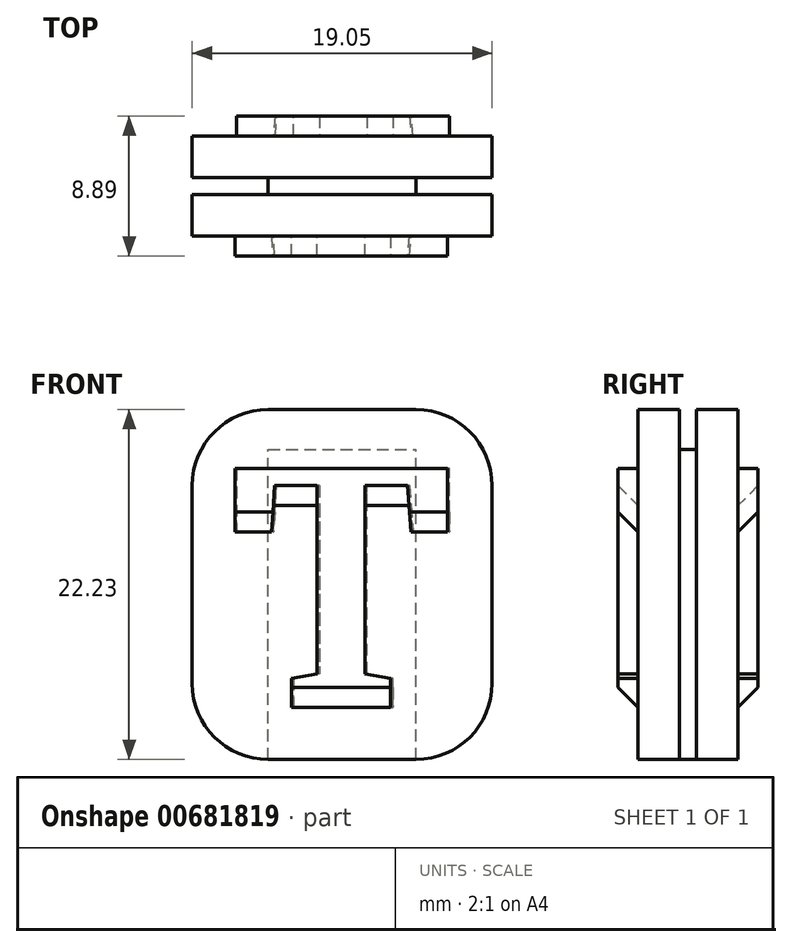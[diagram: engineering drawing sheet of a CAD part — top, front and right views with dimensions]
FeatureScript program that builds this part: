
annotation { "Feature Type Name" : "Feature", "Feature Type Description" : "" }
export const myFeature = defineFeature(function(context is Context, id is Id, definition is map)
    precondition{}
    {
        {
            var Q0;
            Q0=qCreatedBy(makeId("Front.planeOp"),FACE);
            var sketch = newSketch(context, id + "F0", { "sketchPlane" : qUnion([Q0])});
            skLineSegment(sketch, "E0.bottom", {"start": v(0, 0) * mm, "end": v(19.05, 0) * mm});
            skLineSegment(sketch, "E0.top", {"start": v(0, 22.23) * mm, "end": v(19.05, 22.23) * mm});
            skLineSegment(sketch, "E0.left", {"start": v(0, 0) * mm, "end": v(0, 22.23) * mm});
            skLineSegment(sketch, "E0.right", {"start": v(19.05, 0) * mm, "end": v(19.05, 22.23) * mm});
            skSolve(sketch);
        }
        {
            var Q0;
            Q0=makeQuery(id+"F0.imprint","IMPRINT",FACE,{"disambiguationData":[TD([[makeQuery(id+"F0.imprint","IMPRINT",EDGE,{"derivedFrom":sQuery(id+"F0.wireOp",EDGE,"E0.bottom")}),1.0]])]});
            extrude(context, id + "F1", {"entities" : qUnion([Q0]), "depth" : 6.35 * mm, "offsetDistance" : 25.4 * mm});
        }
        {
            var Q0;
            Q0=makeQuery(id+"F1.opExtrude","CAP_FACE",FACE,{"disambiguationData":[OSD([sQuery(id+"F0.wireOp",EDGE,"E0.bottom"),sQuery(id+"F0.wireOp",EDGE,"E0.top"),sQuery(id+"F0.wireOp",EDGE,"E0.left"),sQuery(id+"F0.wireOp",EDGE,"E0.right")])],"isStart":false});
            var sketch = newSketch(context, id + "F2", { "sketchPlane" : qUnion([Q0])});
            skText(sketch, "E1", { "text": "T", "fontName": "RobotoSlab-Bold.ttf"});
            skPoint(sketch, "E2", {"position": v(19.05, 11.11) * mm});
            const initialGuessF2  = {"E1": [0.00229, 0.00331, 1, 0, 0.01536]};
            skSetInitialGuess(sketch, initialGuessF2);
            skSolve(sketch);
        }
        {
            var Q0;
            Q0=makeQuery(id+"F1.opExtrude","CAP_FACE",FACE,{"disambiguationData":[OSD([sQuery(id+"F0.wireOp",EDGE,"E0.bottom"),sQuery(id+"F0.wireOp",EDGE,"E0.top"),sQuery(id+"F0.wireOp",EDGE,"E0.left"),sQuery(id+"F0.wireOp",EDGE,"E0.right")])],"isStart":true});
            var sketch = newSketch(context, id + "F3", { "sketchPlane" : qUnion([Q0])});
            skText(sketch, "E3", { "text": "T", "fontName": "RobotoSlab-Bold.ttf"});
            const initialGuessF3  = {"E3": [-0.01676, 0.00331, 1, 0, 0.01536]};
            skSetInitialGuess(sketch, initialGuessF3);
            skSolve(sketch);
        }
        {
            var Q0;
            Q0=makeQuery(id+"F1.opExtrude","SWEPT_FACE",FACE,{"disambiguationData":[OSD([sQuery(id+"F0.wireOp",EDGE,"E0.top")])]});
            var sketch = newSketch(context, id + "F4", { "sketchPlane" : qUnion([Q0])});
            skLineSegment(sketch, "E4.bottom", {"start": v(0, -2.64) * mm, "end": v(19.05, -2.64) * mm});
            skLineSegment(sketch, "E4.top", {"start": v(0, -3.7) * mm, "end": v(19.05, -3.7) * mm});
            skLineSegment(sketch, "E4.left", {"start": v(0, -2.64) * mm, "end": v(0, -3.7) * mm});
            skLineSegment(sketch, "E4.right", {"start": v(19.05, -2.64) * mm, "end": v(19.05, -3.7) * mm});
            skLineSegment(sketch, "E5", {"start": v(4.83, -2.64) * mm, "end": v(4.83, -3.7) * mm});
            skLineSegment(sketch, "E6", {"start": v(14.22, -2.64) * mm, "end": v(14.22, -3.7) * mm});
            skSolve(sketch);
        }
        {
            var Q0;
            {var subQ0=sQuery(id+"F4.wireOp",EDGE,"E4.left");Q0=makeQuery(id+"F4.imprint","IMPRINT",FACE,{"disambiguationData":[TD([[makeQuery(id+"F4.imprint","IMPRINT",EDGE,{"derivedFrom":subQ0}),-1.0]])]});}
            var Q1;
            {var subQ0=sQuery(id+"F4.wireOp",EDGE,"E4.right");Q1=makeQuery(id+"F4.imprint","IMPRINT",FACE,{"disambiguationData":[TD([[makeQuery(id+"F4.imprint","IMPRINT",EDGE,{"derivedFrom":subQ0}),1.0]])]});}
            extrude(context, id + "F5", {"entities" : qUnion([Q0, Q1]), "operationType" : NewBodyOperationType.REMOVE, "oppositeDirection" : true, "depth" : 25.4 * mm, "offsetDistance" : 25.4 * mm});
        }
        {
            var Q0;
            Q0=makeQuery(id+"F1.opExtrude","SWEPT_FACE",FACE,{"disambiguationData":[OSD([sQuery(id+"F0.wireOp",EDGE,"E0.top")])]});
            var sketch = newSketch(context, id + "F6", { "sketchPlane" : qUnion([Q0])});
            skLineSegment(sketch, "E7.bottom", {"start": v(4.83, -2.64) * mm, "end": v(14.22, -2.64) * mm});
            skLineSegment(sketch, "E7.top", {"start": v(4.83, -3.7) * mm, "end": v(14.22, -3.7) * mm});
            skLineSegment(sketch, "E7.left", {"start": v(4.83, -2.64) * mm, "end": v(4.83, -3.7) * mm});
            skLineSegment(sketch, "E7.right", {"start": v(14.22, -2.64) * mm, "end": v(14.22, -3.7) * mm});
            skSolve(sketch);
        }
        {
            var Q0;
            Q0=makeQuery(id+"F6.imprint","IMPRINT",FACE,{"disambiguationData":[TD([[makeQuery(id+"F6.imprint","IMPRINT",EDGE,{"derivedFrom":sQuery(id+"F6.wireOp",EDGE,"E7.bottom")}),-1.0]])]});
            extrude(context, id + "F7", {"entities" : qUnion([Q0]), "operationType" : NewBodyOperationType.REMOVE, "oppositeDirection" : true, "depth" : 2.54 * mm, "offsetDistance" : 25.4 * mm});
        }
        {
            var Q0;
            {var subQ0=sQuery(id+"F0.wireOp",EDGE,"E0.bottom");var subQ1=sQuery(id+"F0.wireOp",EDGE,"E0.left");var subQ3=sQuery(id+"F4.wireOp",EDGE,"E4.bottom");Q0=makeQuery(id+"F5.boolean.opBoolean","SPLIT",EDGE,{"disambiguationData":[TD([makeQuery(id+"F5.opExtrude","SWEPT_FACE",FACE,{"disambiguationData":[OSD([subQ3]),TDD([makeQuery(id+"F4.imprint","IMPRINT",EDGE,{"disambiguationData":[TD([[makeQuery(id+"F4.imprint","INTERSECT",VERTEX,{"derivedFrom":[subQ3,sQuery(id+"F4.wireOp",EDGE,"E5")]}),1.0]])],"derivedFrom":subQ3})])]})])],"derivedFrom":makeQuery(id+"F1.opExtrude","SWEPT_EDGE",EDGE,{"disambiguationData":[OSD([subQ0,subQ1])]})});}
            var Q1;
            {var subQ0=sQuery(id+"F0.wireOp",EDGE,"E0.bottom");var subQ1=sQuery(id+"F0.wireOp",EDGE,"E0.left");var subQ3=sQuery(id+"F4.wireOp",EDGE,"E4.top");Q1=makeQuery(id+"F5.boolean.opBoolean","SPLIT",EDGE,{"disambiguationData":[TD([makeQuery(id+"F5.opExtrude","SWEPT_FACE",FACE,{"disambiguationData":[OSD([subQ3]),TDD([makeQuery(id+"F4.imprint","IMPRINT",EDGE,{"disambiguationData":[TD([[makeQuery(id+"F4.imprint","INTERSECT",VERTEX,{"derivedFrom":[subQ3,sQuery(id+"F4.wireOp",EDGE,"E5")]}),1.0]])],"derivedFrom":subQ3})])]})])],"derivedFrom":makeQuery(id+"F1.opExtrude","SWEPT_EDGE",EDGE,{"disambiguationData":[OSD([subQ0,subQ1])]})});}
            var Q2;
            {var subQ0=sQuery(id+"F0.wireOp",EDGE,"E0.left");var subQ1=sQuery(id+"F0.wireOp",EDGE,"E0.top");var subQ2=sQuery(id+"F4.wireOp",EDGE,"E4.top");var subQ3=makeQuery(id+"F1.opExtrude","SWEPT_EDGE",EDGE,{"disambiguationData":[OSD([subQ1,subQ0])]});Q2=makeQuery(id+"F5.boolean.opBoolean","SPLIT",EDGE,{"disambiguationData":[TD([makeQuery(id+"F5.opExtrude","SWEPT_FACE",FACE,{"disambiguationData":[OSD([subQ2]),TDD([makeQuery(id+"F4.imprint","IMPRINT",EDGE,{"disambiguationData":[TD([[makeQuery(id+"F4.imprint","INTERSECT",VERTEX,{"derivedFrom":[subQ2,sQuery(id+"F4.wireOp",EDGE,"E5")]}),1.0]])],"derivedFrom":subQ2})])]})])],"derivedFrom":subQ3});}
            var Q3;
            {var subQ0=sQuery(id+"F0.wireOp",EDGE,"E0.left");var subQ1=sQuery(id+"F0.wireOp",EDGE,"E0.top");var subQ2=sQuery(id+"F4.wireOp",EDGE,"E4.bottom");var subQ3=makeQuery(id+"F1.opExtrude","SWEPT_EDGE",EDGE,{"disambiguationData":[OSD([subQ1,subQ0])]});Q3=makeQuery(id+"F5.boolean.opBoolean","SPLIT",EDGE,{"disambiguationData":[TD([makeQuery(id+"F5.opExtrude","SWEPT_FACE",FACE,{"disambiguationData":[OSD([subQ2]),TDD([makeQuery(id+"F4.imprint","IMPRINT",EDGE,{"disambiguationData":[TD([[makeQuery(id+"F4.imprint","INTERSECT",VERTEX,{"derivedFrom":[subQ2,sQuery(id+"F4.wireOp",EDGE,"E5")]}),1.0]])],"derivedFrom":subQ2})])]})])],"derivedFrom":subQ3});}
            var Q4;
            {var subQ0=sQuery(id+"F0.wireOp",EDGE,"E0.right");var subQ1=sQuery(id+"F0.wireOp",EDGE,"E0.top");var subQ2=sQuery(id+"F4.wireOp",EDGE,"E4.bottom");var subQ3=makeQuery(id+"F1.opExtrude","SWEPT_EDGE",EDGE,{"disambiguationData":[OSD([subQ1,subQ0])]});Q4=makeQuery(id+"F5.boolean.opBoolean","SPLIT",EDGE,{"disambiguationData":[TD([makeQuery(id+"F5.opExtrude","SWEPT_FACE",FACE,{"disambiguationData":[OSD([subQ2]),TDD([makeQuery(id+"F4.imprint","IMPRINT",EDGE,{"disambiguationData":[TD([[makeQuery(id+"F4.imprint","INTERSECT",VERTEX,{"derivedFrom":[subQ2,sQuery(id+"F4.wireOp",EDGE,"E6")]}),-1.0]])],"derivedFrom":subQ2})])]})])],"derivedFrom":subQ3});}
            var Q5;
            {var subQ0=sQuery(id+"F0.wireOp",EDGE,"E0.right");var subQ1=sQuery(id+"F0.wireOp",EDGE,"E0.top");var subQ2=sQuery(id+"F4.wireOp",EDGE,"E4.top");var subQ3=makeQuery(id+"F1.opExtrude","SWEPT_EDGE",EDGE,{"disambiguationData":[OSD([subQ1,subQ0])]});Q5=makeQuery(id+"F5.boolean.opBoolean","SPLIT",EDGE,{"disambiguationData":[TD([makeQuery(id+"F5.opExtrude","SWEPT_FACE",FACE,{"disambiguationData":[OSD([subQ2]),TDD([makeQuery(id+"F4.imprint","IMPRINT",EDGE,{"disambiguationData":[TD([[makeQuery(id+"F4.imprint","INTERSECT",VERTEX,{"derivedFrom":[subQ2,sQuery(id+"F4.wireOp",EDGE,"E6")]}),-1.0]])],"derivedFrom":subQ2})])]})])],"derivedFrom":subQ3});}
            var Q6;
            {var subQ0=sQuery(id+"F0.wireOp",EDGE,"E0.bottom");var subQ1=sQuery(id+"F0.wireOp",EDGE,"E0.right");var subQ3=sQuery(id+"F4.wireOp",EDGE,"E4.top");Q6=makeQuery(id+"F5.boolean.opBoolean","SPLIT",EDGE,{"disambiguationData":[TD([makeQuery(id+"F5.opExtrude","SWEPT_FACE",FACE,{"disambiguationData":[OSD([subQ3]),TDD([makeQuery(id+"F4.imprint","IMPRINT",EDGE,{"disambiguationData":[TD([[makeQuery(id+"F4.imprint","INTERSECT",VERTEX,{"derivedFrom":[subQ3,sQuery(id+"F4.wireOp",EDGE,"E6")]}),-1.0]])],"derivedFrom":subQ3})])]})])],"derivedFrom":makeQuery(id+"F1.opExtrude","SWEPT_EDGE",EDGE,{"disambiguationData":[OSD([subQ0,subQ1])]})});}
            var Q7;
            {var subQ0=sQuery(id+"F0.wireOp",EDGE,"E0.bottom");var subQ1=sQuery(id+"F0.wireOp",EDGE,"E0.right");var subQ3=sQuery(id+"F4.wireOp",EDGE,"E4.bottom");Q7=makeQuery(id+"F5.boolean.opBoolean","SPLIT",EDGE,{"disambiguationData":[TD([makeQuery(id+"F5.opExtrude","SWEPT_FACE",FACE,{"disambiguationData":[OSD([subQ3]),TDD([makeQuery(id+"F4.imprint","IMPRINT",EDGE,{"disambiguationData":[TD([[makeQuery(id+"F4.imprint","INTERSECT",VERTEX,{"derivedFrom":[subQ3,sQuery(id+"F4.wireOp",EDGE,"E6")]}),-1.0]])],"derivedFrom":subQ3})])]})])],"derivedFrom":makeQuery(id+"F1.opExtrude","SWEPT_EDGE",EDGE,{"disambiguationData":[OSD([subQ0,subQ1])]})});}
            fillet(context, id + "F8", {"entities" : qUnion([Q0, Q1, Q2, Q3, Q4, Q5, Q6, Q7]), "radius" : 4.83 * mm, "tangentPropagation" : true, "allowEdgeOverflow" : false});
        }
        {
            var Q0;
            Q0=makeQuery(id+"F3.imprint","IMPRINT",FACE,{"disambiguationData":[TD([[makeQuery(id+"F3.imprint","IMPRINT",EDGE,{"derivedFrom":sQuery(id+"F3.wireOp",EDGE,"E3.sketch_text.stroke-0")}),-1.0]])]});
            extrude(context, id + "F9", {"entities" : qUnion([Q0]), "operationType" : NewBodyOperationType.ADD, "depth" : 1.27 * mm, "offsetDistance" : 25.4 * mm});
        }
        {
            var Q0;
            Q0=makeQuery(id+"F2.imprint","IMPRINT",FACE,{"disambiguationData":[TD([[makeQuery(id+"F2.imprint","IMPRINT",EDGE,{"derivedFrom":sQuery(id+"F2.wireOp",EDGE,"E1.sketch_text.stroke-0")}),-1.0]])]});
            extrude(context, id + "F10", {"entities" : qUnion([Q0]), "operationType" : NewBodyOperationType.ADD, "depth" : 1.27 * mm, "offsetDistance" : 25.4 * mm});
        }
        {
            var Q0;
            Q0=makeQuery(id+"F9.opExtrude","CAP_EDGE",EDGE,{"disambiguationData":[OSD([sQuery(id+"F3.wireOp",EDGE,"E3.sketch_text.stroke-13")])],"isStart":false});
            var Q1;
            Q1=makeQuery(id+"F9.opExtrude","CAP_EDGE",EDGE,{"disambiguationData":[OSD([sQuery(id+"F3.wireOp",EDGE,"E3.sketch_text.stroke-11")])],"isStart":false});
            var Q2;
            Q2=makeQuery(id+"F9.opExtrude","CAP_EDGE",EDGE,{"disambiguationData":[OSD([sQuery(id+"F3.wireOp",EDGE,"E3.sketch_text.stroke-3")])],"isStart":false});
            var Q3;
            Q3=makeQuery(id+"F9.opExtrude","CAP_EDGE",EDGE,{"disambiguationData":[OSD([sQuery(id+"F3.wireOp",EDGE,"E3.sketch_text.stroke-1")])],"isStart":false});
            var Q4;
            Q4=makeQuery(id+"F9.opExtrude","CAP_EDGE",EDGE,{"disambiguationData":[OSD([sQuery(id+"F3.wireOp",EDGE,"E3.sketch_text.stroke-7")])],"isStart":false});
            chamfer(context, id + "F11", {"entities" : qUnion([Q0, Q1, Q2, Q3, Q4]), "width" : 1.27 * mm, "tangentPropagation" : true});
        }
        {
            var Q0;
            Q0=makeQuery(id+"F10.opExtrude","CAP_EDGE",EDGE,{"disambiguationData":[OSD([sQuery(id+"F2.wireOp",EDGE,"E1.sketch_text.stroke-13")])],"isStart":false});
            var Q1;
            Q1=makeQuery(id+"F10.opExtrude","CAP_EDGE",EDGE,{"disambiguationData":[OSD([sQuery(id+"F2.wireOp",EDGE,"E1.sketch_text.stroke-11")])],"isStart":false});
            var Q2;
            Q2=makeQuery(id+"F10.opExtrude","CAP_EDGE",EDGE,{"disambiguationData":[OSD([sQuery(id+"F2.wireOp",EDGE,"E1.sketch_text.stroke-3")])],"isStart":false});
            var Q3;
            Q3=makeQuery(id+"F10.opExtrude","CAP_EDGE",EDGE,{"disambiguationData":[OSD([sQuery(id+"F2.wireOp",EDGE,"E1.sketch_text.stroke-1")])],"isStart":false});
            var Q4;
            Q4=makeQuery(id+"F10.opExtrude","CAP_EDGE",EDGE,{"disambiguationData":[OSD([sQuery(id+"F2.wireOp",EDGE,"E1.sketch_text.stroke-7")])],"isStart":false});
            chamfer(context, id + "F12", {"entities" : qUnion([Q0, Q1, Q2, Q3, Q4]), "width" : 1.27 * mm, "tangentPropagation" : true});
        }
    });
